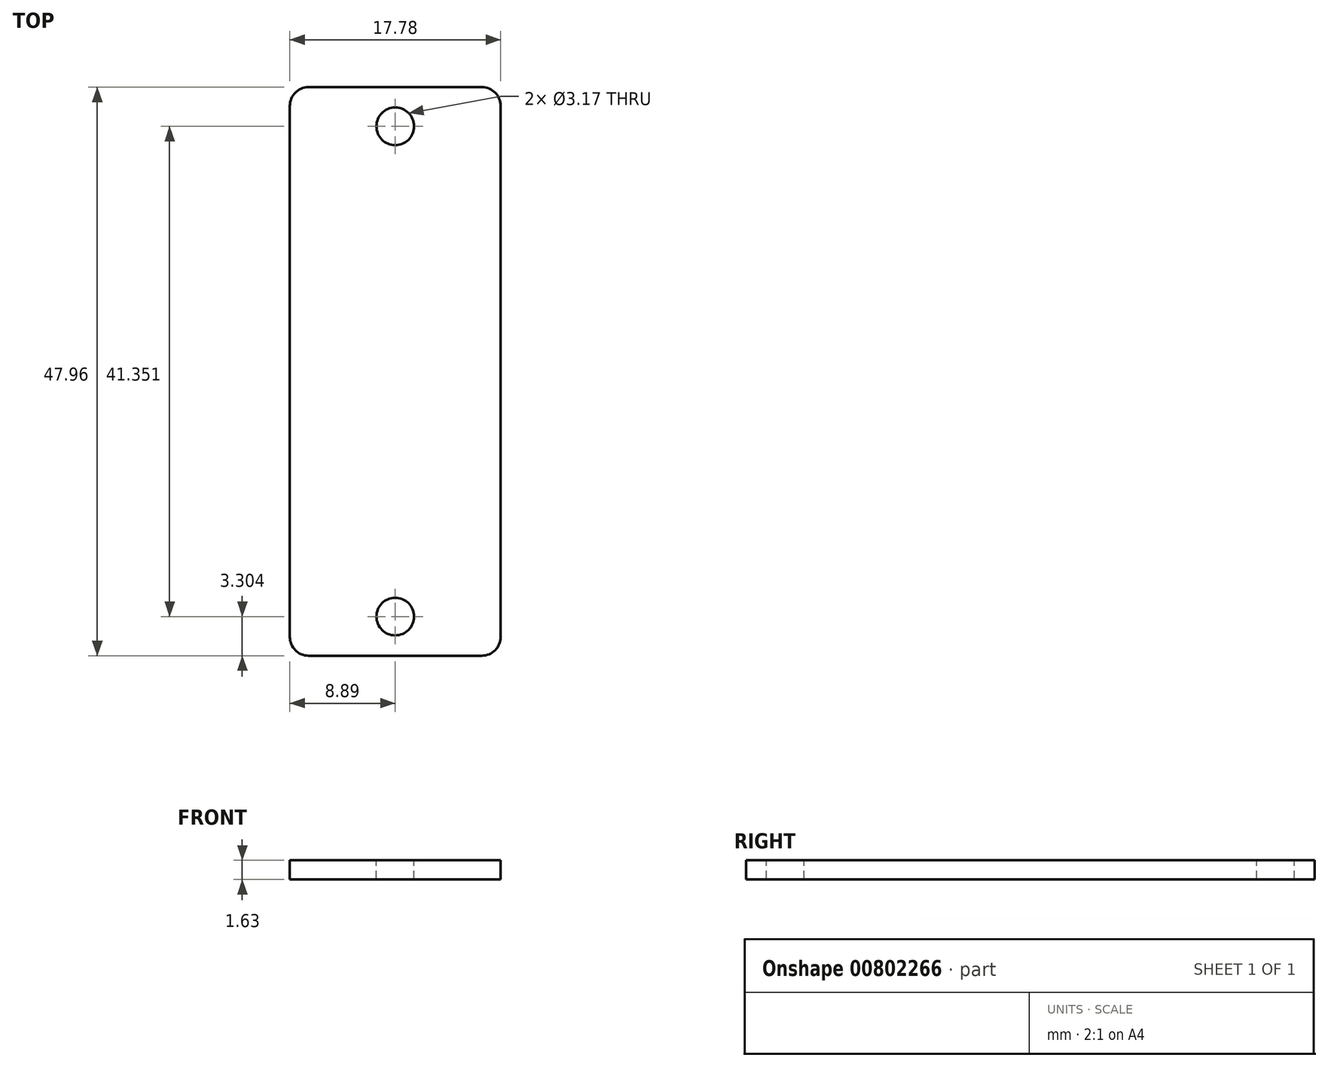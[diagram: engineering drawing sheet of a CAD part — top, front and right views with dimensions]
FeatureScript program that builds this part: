
annotation { "Feature Type Name" : "Feature", "Feature Type Description" : "" }
export const myFeature = defineFeature(function(context is Context, id is Id, definition is map)
    precondition{}
    {
        {
            var Q0;
            Q0=qCreatedBy(makeId("Top.planeOp"),FACE);
            var sketch = newSketch(context, id + "F0", { "sketchPlane" : qUnion([Q0])});
            skLineSegment(sketch, "E0.bottom", {"start": v(7.3, -23.98) * mm, "end": v(-7.3, -23.98) * mm});
            skLineSegment(sketch, "E0.top", {"start": v(7.3, 23.98) * mm, "end": v(-7.3, 23.98) * mm});
            skLineSegment(sketch, "E0.left", {"start": v(8.89, -22.4) * mm, "end": v(8.9, 22.4) * mm});
            skLineSegment(sketch, "E0.right", {"start": v(-8.9, -22.4) * mm, "end": v(-8.89, 22.4) * mm});
            skPoint(sketch, "E0.middle", {"position": v(0, 0) * mm});
            skPoint(sketch, "E1.visualSharp", {"position": v(-8.89, 23.98) * mm});
            skArc(sketch, "E1.filletArc", {"start": v(-7.3, 23.98) * mm, "mid": v(-8.43, 23.51) * mm, "end": v(-8.89, 22.4) * mm});
            skPoint(sketch, "E2.visualSharp", {"position": v(8.9, 23.98) * mm});
            skArc(sketch, "E2.filletArc", {"start": v(8.9, 22.4) * mm, "mid": v(8.43, 23.51) * mm, "end": v(7.3, 23.98) * mm});
            skPoint(sketch, "E3.visualSharp", {"position": v(8.89, -23.98) * mm});
            skArc(sketch, "E3.filletArc", {"start": v(7.3, -23.98) * mm, "mid": v(8.43, -23.51) * mm, "end": v(8.9, -22.4) * mm});
            skPoint(sketch, "E4.visualSharp", {"position": v(-8.9, -23.98) * mm});
            skArc(sketch, "E4.filletArc", {"start": v(-8.9, -22.4) * mm, "mid": v(-8.43, -23.51) * mm, "end": v(-7.3, -23.98) * mm});
            skCircle(sketch, "E5", {"center": v(0, 20.68) * mm, "radius": 1.59 * mm});
            skCircle(sketch, "E6.MirrorC", {"center": v(0, -20.68) * mm, "radius": 1.59 * mm});
            skSolve(sketch);
        }
        {
            var Q0;
            Q0=makeQuery(id+"F0.imprint","IMPRINT",FACE,{"disambiguationData":[TD([[makeQuery(id+"F0.imprint","IMPRINT",EDGE,{"derivedFrom":sQuery(id+"F0.wireOp",EDGE,"E0.bottom")}),-1.0]])]});
            extrude(context, id + "F1", {"entities" : qUnion([Q0]), "oppositeDirection" : true, "depth" : 1.63 * mm, "offsetDistance" : 25.4 * mm});
        }
    });
